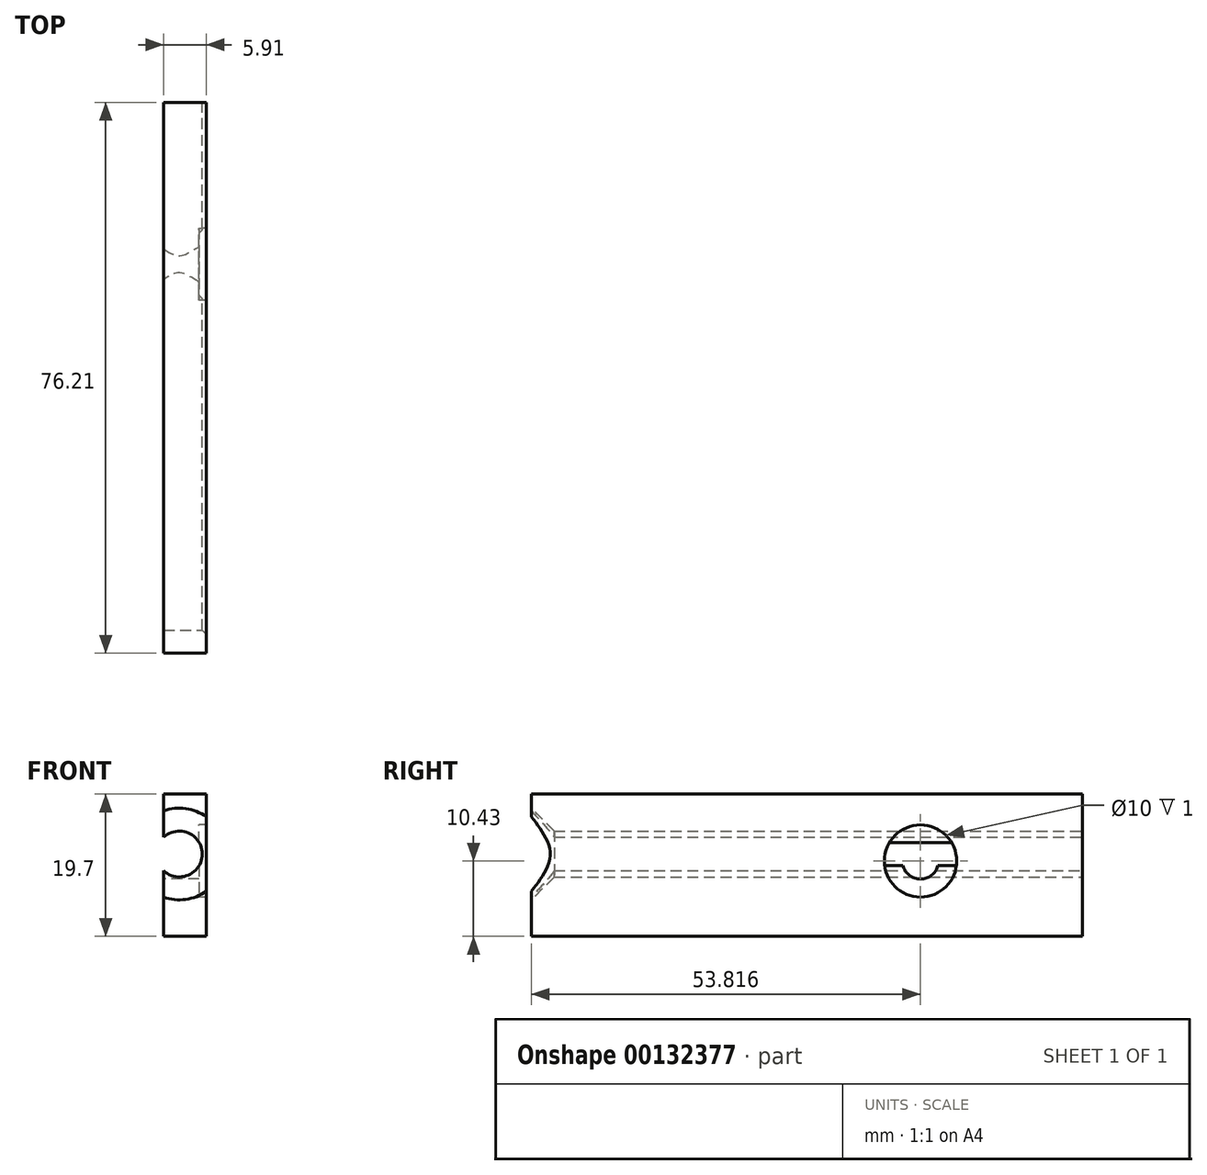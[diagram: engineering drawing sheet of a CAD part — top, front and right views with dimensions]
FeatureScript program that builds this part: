
annotation { "Feature Type Name" : "Feature", "Feature Type Description" : "" }
export const myFeature = defineFeature(function(context is Context, id is Id, definition is map)
    precondition{}
    {
        {
            var Q0;
            Q0=qCreatedBy(makeId("Front.planeOp"),FACE);
            var sketch = newSketch(context, id + "F0", { "sketchPlane" : qUnion([Q0])});
            skLineSegment(sketch, "E0.bottom", {"start": v(23.41, 0) * mm, "end": v(0, 0) * mm});
            skLineSegment(sketch, "E0.top", {"start": v(23.41, 0) * mm, "end": v(0, 0) * mm});
            skLineSegment(sketch, "E0.left", {"start": v(23.41, 0) * mm, "end": v(23.41, 0) * mm});
            skLineSegment(sketch, "E0.right", {"start": v(0, 0) * mm, "end": v(0, 0) * mm});
            skLineSegment(sketch, "E1.bottom", {"start": v(52.33, 32.82) * mm, "end": v(17.44, 32.82) * mm});
            skLineSegment(sketch, "E1.top", {"start": v(52.33, 30.53) * mm, "end": v(17.44, 30.53) * mm});
            skLineSegment(sketch, "E1.left", {"start": v(52.33, 32.82) * mm, "end": v(52.33, 30.53) * mm});
            skLineSegment(sketch, "E1.right", {"start": v(17.44, 32.82) * mm, "end": v(17.44, 30.53) * mm});
            skLineSegment(sketch, "E2.bottom", {"start": v(54.63, 15.38) * mm, "end": v(60.14, 15.38) * mm});
            skLineSegment(sketch, "E2.top", {"start": v(54.63, 20.43) * mm, "end": v(60.14, 20.43) * mm});
            skLineSegment(sketch, "E2.left", {"start": v(54.63, 15.38) * mm, "end": v(54.63, 20.43) * mm});
            skLineSegment(sketch, "E2.right", {"start": v(60.14, 15.38) * mm, "end": v(60.14, 20.43) * mm});
            skLineSegment(sketch, "E3.bottom", {"start": v(82.3, 37.38) * mm, "end": v(88.2, 37.38) * mm});
            skLineSegment(sketch, "E3.top", {"start": v(82.3, 17.68) * mm, "end": v(88.2, 17.68) * mm});
            skLineSegment(sketch, "E3.left", {"start": v(82.3, 37.38) * mm, "end": v(82.3, 17.68) * mm});
            skLineSegment(sketch, "E3.right", {"start": v(88.2, 37.38) * mm, "end": v(88.2, 17.68) * mm});
            skSolve(sketch);
        }
        {
            var Q0;
            Q0=makeQuery(id+"F0.imprint","IMPRINT",FACE,{"disambiguationData":[TD([[makeQuery(id+"F0.imprint","IMPRINT",EDGE,{"derivedFrom":sQuery(id+"F0.wireOp",EDGE,"E3.bottom")}),-1.0]])]});
            var Q1;
            Q1=sQuery(id+"F0.wireOp",EDGE,"E3.left");
            var Q2;
            Q2=sQuery(id+"F0.wireOp",EDGE,"E3.top");
            var Q3;
            Q3=sQuery(id+"F0.wireOp",EDGE,"E3.right");
            var Q4;
            Q4=sQuery(id+"F0.wireOp",EDGE,"E3.bottom");
            extrude(context, id + "F1", {"entities" : qUnion([Q0]), "surfaceEntities" : qUnion([Q1, Q2, Q3, Q4]), "depth" : 76.2 * mm});
        }
        {
            var Q0;
            Q0=makeQuery(id+"F1.opExtrude","CAP_FACE",FACE,{"disambiguationData":[OSD([sQuery(id+"F0.wireOp",EDGE,"E3.bottom"),sQuery(id+"F0.wireOp",EDGE,"E3.top"),sQuery(id+"F0.wireOp",EDGE,"E3.left"),sQuery(id+"F0.wireOp",EDGE,"E3.right")])],"isStart":false});
            var sketch = newSketch(context, id + "F2", { "sketchPlane" : qUnion([Q0])});
            skPoint(sketch, "E4", {"position": v(84.47, 29.08) * mm});
            skSolve(sketch);
        }
        {
            var Q0;
            Q0=sQuery(id+"F2.wireOp",VERTEX,"E4");
            var Q1;
            Q1=makeQuery(id+"F1.opExtrude","SWEPT_BODY",BODY,{"disambiguationData":[OSD([sQuery(id+"F0.wireOp",EDGE,"E3.bottom"),sQuery(id+"F0.wireOp",EDGE,"E3.top"),sQuery(id+"F0.wireOp",EDGE,"E3.left"),sQuery(id+"F0.wireOp",EDGE,"E3.right")])]});
            hole(context, id + "F3", {"style" : HoleStyle.C_SINK, "endStyle" : HoleEndStyle.THROUGH, "holeDiameter" : 6.35 * mm, "cSinkDiameter" : 12.7 * mm, "cSinkAngle" : 90 * degree, "locations" : qUnion([Q0]), "scope" : qUnion([Q1]), "isTappedThrough" : true});
        }
        {
            var Q0;
            Q0=makeQuery(id+"F1.opExtrude","SWEPT_FACE",FACE,{"disambiguationData":[OSD([sQuery(id+"F0.wireOp",EDGE,"E3.right")])]});
            var sketch = newSketch(context, id + "F4", { "sketchPlane" : qUnion([Q0])});
            skPoint(sketch, "E5", {"position": v(-22.38, 28.11) * mm});
            skSolve(sketch);
        }
        {
            var Q0;
            Q0=sQuery(id+"F4.wireOp",VERTEX,"E5");
            var Q1;
            Q1=makeQuery(id+"F1.opExtrude","SWEPT_BODY",BODY,{"disambiguationData":[OSD([sQuery(id+"F0.wireOp",EDGE,"E3.bottom"),sQuery(id+"F0.wireOp",EDGE,"E3.top"),sQuery(id+"F0.wireOp",EDGE,"E3.left"),sQuery(id+"F0.wireOp",EDGE,"E3.right")])]});
            hole(context, id + "F5", {"style" : HoleStyle.C_BORE, "endStyle" : HoleEndStyle.THROUGH, "holeDiameter" : 5 * mm, "cBoreDiameter" : 10 * mm, "cBoreDepth" : 1 * mm, "locations" : qUnion([Q0]), "scope" : qUnion([Q1]), "isTappedThrough" : true});
        }
    });
